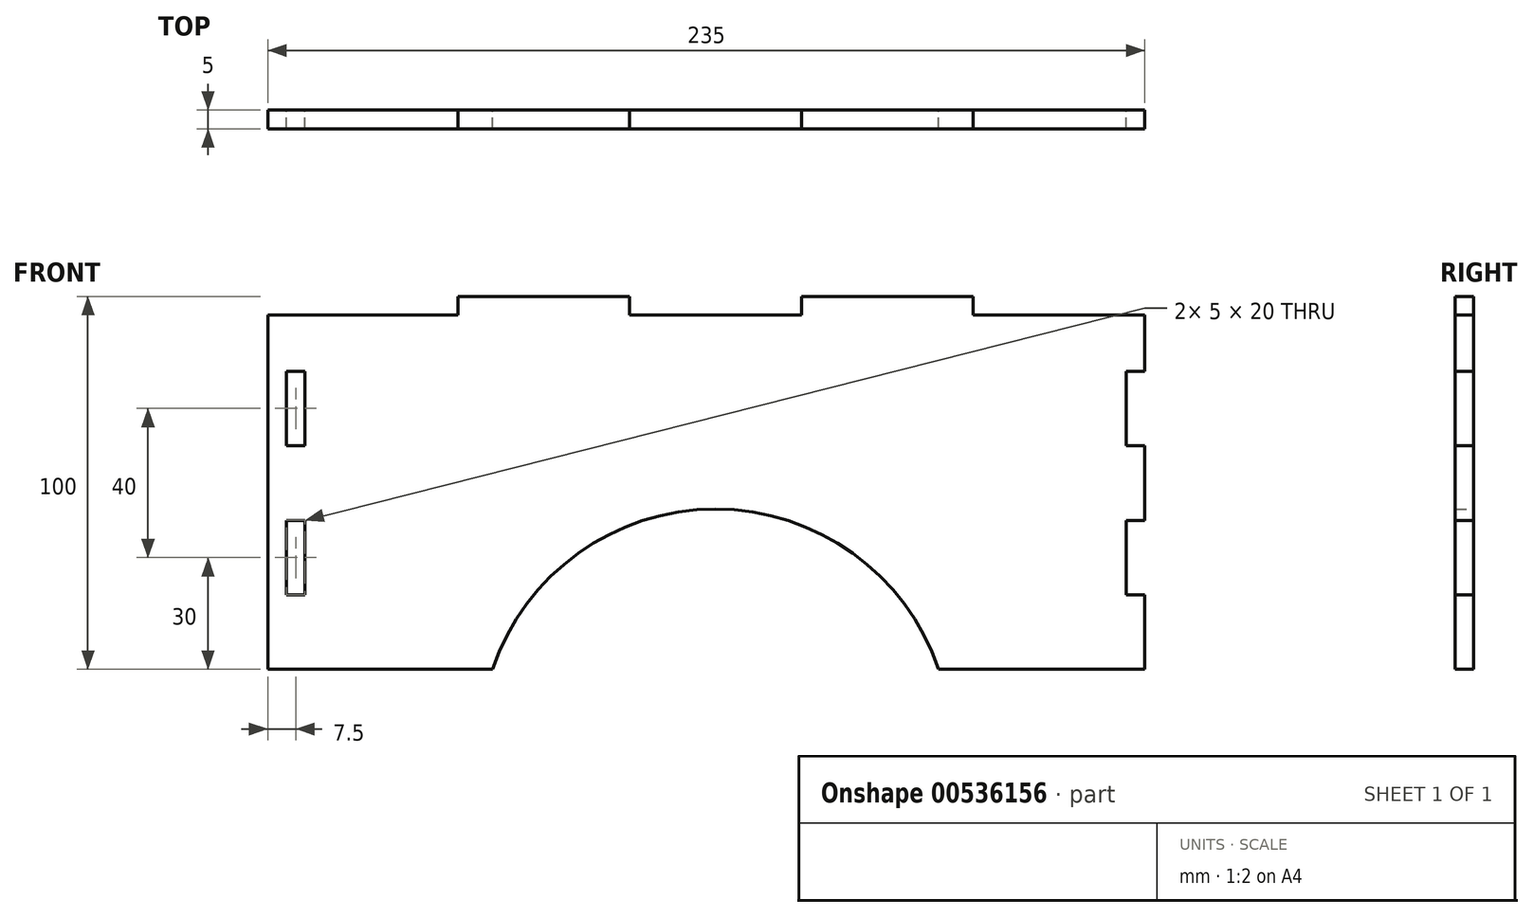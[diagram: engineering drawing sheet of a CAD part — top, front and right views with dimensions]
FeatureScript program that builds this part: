
annotation { "Feature Type Name" : "Feature", "Feature Type Description" : "" }
export const myFeature = defineFeature(function(context is Context, id is Id, definition is map)
    precondition{}
    {
        {
            var Q0;
            Q0=qCreatedBy(makeId("Front.planeOp"),FACE);
            var sketch = newSketch(context, id + "F0", { "sketchPlane" : qUnion([Q0])});
            skLineSegment(sketch, "E0.top", {"start": v(110, -47.5) * mm, "end": v(59.74, -47.5) * mm});
            skLineSegment(sketch, "E0.left", {"start": v(110, 32.5) * mm, "end": v(110, 12.5) * mm});
            skLineSegment(sketch, "E0.right", {"start": v(-110, 32.5) * mm, "end": v(-110, 12.5) * mm});
            skPoint(sketch, "E0.middle", {"position": v(0, 0) * mm});
            skLineSegment(sketch, "E1", {"start": v(-115, -27.5) * mm, "end": v(-115, -7.5) * mm, "construction": true});
            skLineSegment(sketch, "E2", {"start": v(-69, 52.5) * mm, "end": v(-23, 52.5) * mm, "construction": true});
            skLineSegment(sketch, "E3", {"start": v(115, 47.5) * mm, "end": v(115, -47.5) * mm, "construction": true});
            skArc(sketch, "E4", {"start": v(59.74, -47.5) * mm, "mid": v(0, -4.5) * mm, "end": v(-59.74, -47.5) * mm});
            skLineSegment(sketch, "E5.bottom", {"start": v(-110, -47.5) * mm, "end": v(-59.74, -47.5) * mm, "construction": true});
            skLineSegment(sketch, "E5.top", {"start": v(-110, -132.5) * mm, "end": v(110, -132.5) * mm, "construction": true});
            skLineSegment(sketch, "E5.left", {"start": v(-110, -47.5) * mm, "end": v(-110, -132.5) * mm, "construction": true});
            skLineSegment(sketch, "E5.right", {"start": v(110, -47.5) * mm, "end": v(110, -132.5) * mm, "construction": true});
            skLineSegment(sketch, "E6.trimOffspring", {"start": v(59.74, -47.5) * mm, "end": v(110, -47.5) * mm, "construction": true});
            skLineSegment(sketch, "E7.trimOffspring", {"start": v(-59.74, -47.5) * mm, "end": v(-110, -47.5) * mm});
            skLineSegment(sketch, "E8", {"start": v(-110, -47.5) * mm, "end": v(-115, -47.5) * mm});
            skLineSegment(sketch, "E9", {"start": v(-115, -27.5) * mm, "end": v(-110, -27.5) * mm});
            skLineSegment(sketch, "E10", {"start": v(-110, -7.5) * mm, "end": v(-115, -7.5) * mm});
            skLineSegment(sketch, "E11", {"start": v(-115, 12.5) * mm, "end": v(-110, 12.5) * mm});
            skLineSegment(sketch, "E12", {"start": v(-110, 32.5) * mm, "end": v(-115, 32.5) * mm});
            skLineSegment(sketch, "E13", {"start": v(-69, 52.5) * mm, "end": v(-69, 47.5) * mm});
            skLineSegment(sketch, "E14.trimOffspring", {"start": v(-110, -7.5) * mm, "end": v(-110, -17.5) * mm});
            skPoint(sketch, "E15.orphan", {"position": v(-110, 47.5) * mm});
            skLineSegment(sketch, "E16", {"start": v(-23, 47.5) * mm, "end": v(-23, 52.5) * mm});
            skLineSegment(sketch, "E17.MirrorCS", {"start": v(110, -47.5) * mm, "end": v(115, -47.5) * mm});
            skLineSegment(sketch, "E18.MirrorCS", {"start": v(115, -27.5) * mm, "end": v(110, -27.5) * mm});
            skLineSegment(sketch, "E19.MirrorCS", {"start": v(110, -7.5) * mm, "end": v(115, -7.5) * mm});
            skLineSegment(sketch, "E20.MirrorCS", {"start": v(115, 12.5) * mm, "end": v(110, 12.5) * mm});
            skLineSegment(sketch, "E21.MirrorCS", {"start": v(110, 32.5) * mm, "end": v(115, 32.5) * mm});
            skLineSegment(sketch, "E22.MirrorCS", {"start": v(23, 47.5) * mm, "end": v(23, 52.5) * mm});
            skLineSegment(sketch, "E23.MirrorCS", {"start": v(69, 52.5) * mm, "end": v(69, 47.5) * mm});
            skLineSegment(sketch, "E24", {"start": v(115, 47.5) * mm, "end": v(115, 32.5) * mm});
            skLineSegment(sketch, "E25", {"start": v(115, 12.5) * mm, "end": v(115, -7.5) * mm});
            skPoint(sketch, "E26.orphan", {"position": v(110, 47.5) * mm});
            skLineSegment(sketch, "E27.trimOffspring", {"start": v(110, -7.5) * mm, "end": v(110, -27.5) * mm});
            skLineSegment(sketch, "E28", {"start": v(115, -27.5) * mm, "end": v(115, -47.5) * mm});
            skLineSegment(sketch, "E29", {"start": v(-69, 47.5) * mm, "end": v(-115, 47.5) * mm});
            skLineSegment(sketch, "E30", {"start": v(-69, 52.5) * mm, "end": v(-23, 52.5) * mm});
            skLineSegment(sketch, "E31.trimOffspring", {"start": v(23, 52.5) * mm, "end": v(69, 52.5) * mm, "construction": true});
            skLineSegment(sketch, "E32", {"start": v(-23, 47.5) * mm, "end": v(23, 47.5) * mm});
            skLineSegment(sketch, "E33", {"start": v(23, 52.5) * mm, "end": v(69, 52.5) * mm});
            skLineSegment(sketch, "E34", {"start": v(115, 47.5) * mm, "end": v(69, 47.5) * mm});
            skLineSegment(sketch, "E35.bottom", {"start": v(-115, 47.5) * mm, "end": v(-120, 47.5) * mm});
            skLineSegment(sketch, "E35.top", {"start": v(-115, -47.5) * mm, "end": v(-120, -47.5) * mm});
            skLineSegment(sketch, "E35.left", {"start": v(-115, 32.5) * mm, "end": v(-115, 12.5) * mm});
            skLineSegment(sketch, "E35.right", {"start": v(-120, 47.5) * mm, "end": v(-120, -47.5) * mm});
            skLineSegment(sketch, "E36.trimOffspring", {"start": v(-115, 12.5) * mm, "end": v(-115, 32.5) * mm, "construction": true});
            skLineSegment(sketch, "E37.trimOffspring", {"start": v(-115, -7.5) * mm, "end": v(-115, -27.5) * mm});
            skLineSegment(sketch, "E38", {"start": v(-110, -17.5) * mm, "end": v(-110, -27.5) * mm});
            skSolve(sketch);
        }
        {
            var Q0;
            Q0 = qSketchRegion(id + "F0", true);
            extrude(context, id + "F1", {"entities" : qUnion([Q0]), "depth" : 5 * mm, "offsetDistance" : 25 * mm});
        }
    });
